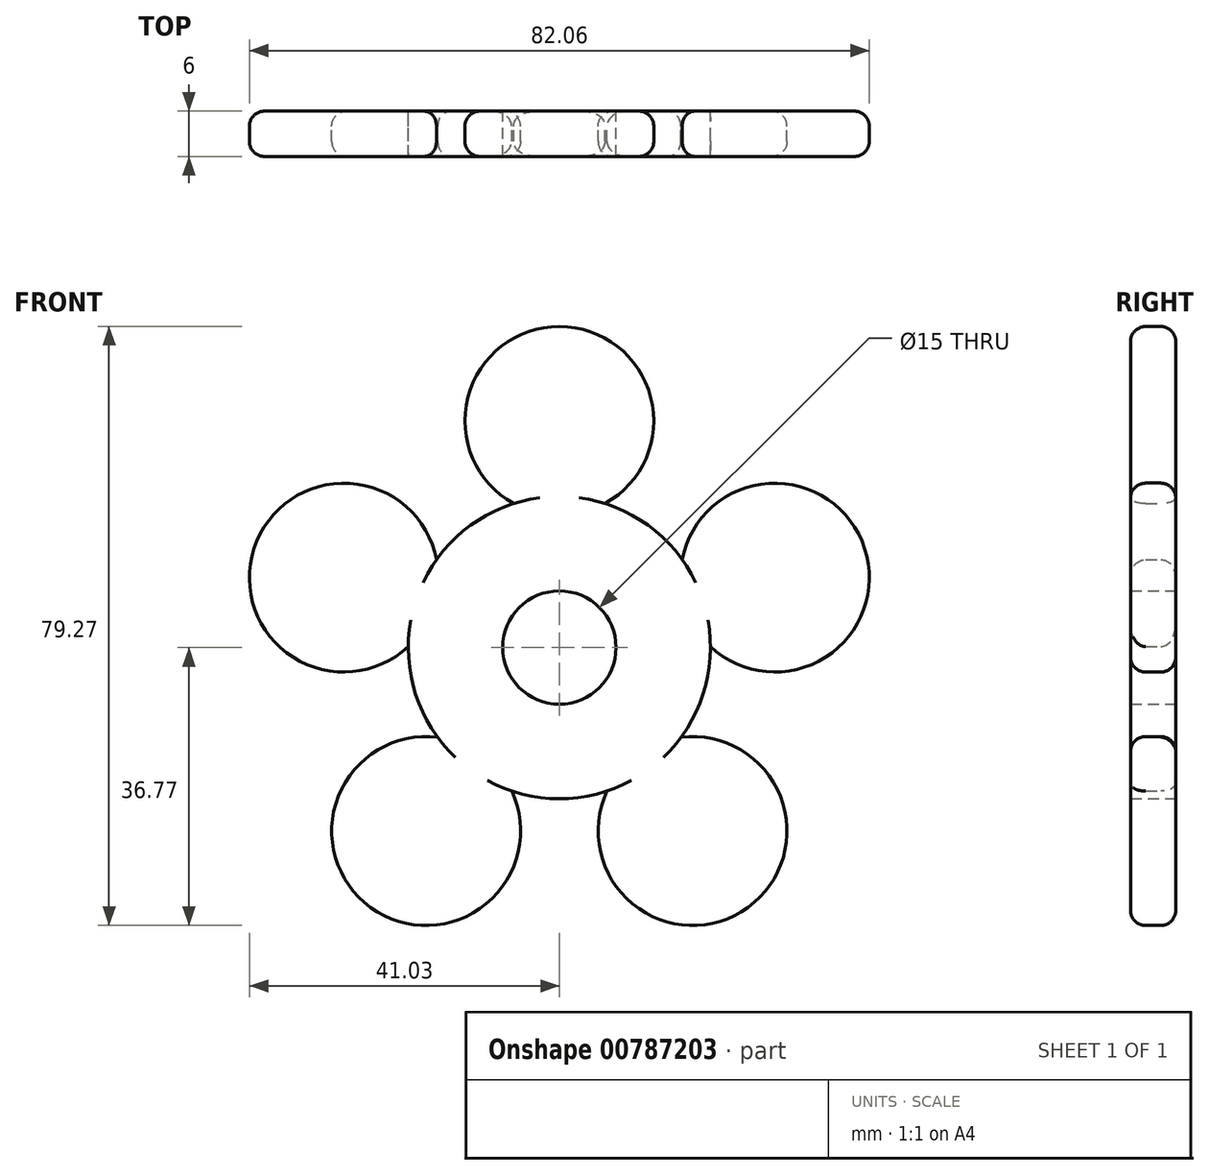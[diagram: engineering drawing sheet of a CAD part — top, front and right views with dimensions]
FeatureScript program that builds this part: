
annotation { "Feature Type Name" : "Feature", "Feature Type Description" : "" }
export const myFeature = defineFeature(function(context is Context, id is Id, definition is map)
    precondition{}
    {
        {
            var Q0;
            Q0=qCreatedBy(makeId("Front.planeOp"),FACE);
            var sketch = newSketch(context, id + "F0", { "sketchPlane" : qUnion([Q0])});
            skArc(sketch, "E0", {"start": v(-12.82, 15.35) * mm, "mid": v(-14.66, 13.6) * mm, "end": v(-16.26, 11.65) * mm});
            skArc(sketch, "E1", {"start": v(6.05, 19.06) * mm, "mid": v(0, 42.5) * mm, "end": v(-6.05, 19.06) * mm});
            skCircle(sketch, "E2", {"center": v(0, 0) * mm, "radius": 7.5 * mm});
            skPoint(sketch, "E3.center.orphan", {"position": v(-45.98, 0) * mm});
            skPoint(sketch, "E4.center.orphan", {"position": v(-75.11, 0) * mm});
            skPoint(sketch, "E5.start.orphan", {"position": v(-51.16, 7.16) * mm});
            skPoint(sketch, "E6.start.orphan", {"position": v(50.58, 7.16) * mm});
            skPoint(sketch, "E7.center.orphan", {"position": v(74.53, 0) * mm});
            skPoint(sketch, "E8.center.orphan", {"position": v(0, -74.68) * mm});
            skArc(sketch, "E9.1.0", {"start": v(-16.26, 11.65) * mm, "mid": v(-40.42, 13.13) * mm, "end": v(-20, 0.14) * mm});
            skArc(sketch, "E9.2.0", {"start": v(-16.1, -11.86) * mm, "mid": v(-24.98, -34.38) * mm, "end": v(-6.3, -18.98) * mm});
            skArc(sketch, "E9.3.0", {"start": v(6.3, -18.98) * mm, "mid": v(24.98, -34.38) * mm, "end": v(16.1, -11.86) * mm});
            skArc(sketch, "E9.4.0", {"start": v(20, 0.14) * mm, "mid": v(40.42, 13.13) * mm, "end": v(16.26, 11.65) * mm});
            skPoint(sketch, "E10.trimOffspring.end.orphan", {"position": v(6.47, 19.3) * mm});
            skPoint(sketch, "E11.trimOffspring.end.orphan", {"position": v(-6.47, 19.3) * mm});
            skArc(sketch, "E12", {"start": v(-12.82, 15.35) * mm, "mid": v(-9.62, 17.54) * mm, "end": v(-6.05, 19.06) * mm});
            skArc(sketch, "E13.trimOffspring", {"start": v(-20, 0.14) * mm, "mid": v(-19.02, -6.18) * mm, "end": v(-16.1, -11.86) * mm});
            skArc(sketch, "E14.trimOffspring", {"start": v(6.05, 19.06) * mm, "mid": v(9.62, 17.54) * mm, "end": v(12.82, 15.35) * mm});
            skArc(sketch, "E15.trimOffspring", {"start": v(-6.3, -18.98) * mm, "mid": v(0, -20) * mm, "end": v(6.3, -18.98) * mm});
            skArc(sketch, "E16.trimOffspring", {"start": v(16.1, -11.86) * mm, "mid": v(19.02, -6.18) * mm, "end": v(20, 0.14) * mm});
            skArc(sketch, "E17.trimOffspring", {"start": v(16.26, 11.65) * mm, "mid": v(14.66, 13.6) * mm, "end": v(12.82, 15.35) * mm});
            skSolve(sketch);
        }
        {
            var Q0;
            Q0=makeQuery(id+"F0.imprint","IMPRINT",FACE,{"disambiguationData":[TD([[makeQuery(id+"F0.imprint","IMPRINT",EDGE,{"derivedFrom":sQuery(id+"F0.wireOp",EDGE,"E0")}),1.0]])]});
            extrude(context, id + "F1", {"entities" : qUnion([Q0]), "depth" : 6 * mm, "offsetDistance" : 25 * mm});
        }
        {
            var Q0;
            Q0=makeQuery(id+"F1.opExtrude","CAP_EDGE",EDGE,{"disambiguationData":[OSD([sQuery(id+"F0.wireOp",EDGE,"E1")])],"isStart":true});
            var Q1;
            Q1=makeQuery(id+"F1.opExtrude","CAP_EDGE",EDGE,{"disambiguationData":[OSD([sQuery(id+"F0.wireOp",EDGE,"E1")])],"isStart":false});
            var Q2;
            Q2=makeQuery(id+"F1.opExtrude","CAP_EDGE",EDGE,{"disambiguationData":[OSD([sQuery(id+"F0.wireOp",EDGE,"E9.1.0")])],"isStart":false});
            var Q3;
            Q3=makeQuery(id+"F1.opExtrude","CAP_EDGE",EDGE,{"disambiguationData":[OSD([sQuery(id+"F0.wireOp",EDGE,"E9.1.0")])],"isStart":true});
            var Q4;
            Q4=makeQuery(id+"F1.opExtrude","CAP_EDGE",EDGE,{"disambiguationData":[OSD([sQuery(id+"F0.wireOp",EDGE,"E9.2.0")])],"isStart":false});
            var Q5;
            Q5=makeQuery(id+"F1.opExtrude","CAP_EDGE",EDGE,{"disambiguationData":[OSD([sQuery(id+"F0.wireOp",EDGE,"E9.2.0")])],"isStart":true});
            var Q6;
            Q6=makeQuery(id+"F1.opExtrude","CAP_EDGE",EDGE,{"disambiguationData":[OSD([sQuery(id+"F0.wireOp",EDGE,"E9.3.0")])],"isStart":false});
            var Q7;
            Q7=makeQuery(id+"F1.opExtrude","CAP_EDGE",EDGE,{"disambiguationData":[OSD([sQuery(id+"F0.wireOp",EDGE,"E9.3.0")])],"isStart":true});
            var Q8;
            Q8=makeQuery(id+"F1.opExtrude","CAP_EDGE",EDGE,{"disambiguationData":[OSD([sQuery(id+"F0.wireOp",EDGE,"E9.4.0")])],"isStart":false});
            var Q9;
            Q9=makeQuery(id+"F1.opExtrude","CAP_EDGE",EDGE,{"disambiguationData":[OSD([sQuery(id+"F0.wireOp",EDGE,"E9.4.0")])],"isStart":true});
            fillet(context, id + "F2", {"entities" : qUnion([Q0, Q1, Q2, Q3, Q4, Q5, Q6, Q7, Q8, Q9]), "radius" : 2 * mm, "tangentPropagation" : true, "allowEdgeOverflow" : false});
        }
    });
